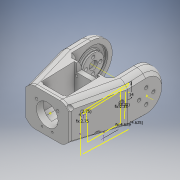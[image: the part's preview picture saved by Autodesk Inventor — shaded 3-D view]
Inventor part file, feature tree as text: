
AUTODESK INVENTOR PART (.ipt)
format: ipt  version: 2018 (Build 220112000, 112)  size: 1,037,312 bytes
history: native  units: mm
features: projected_geometry x48, sketch x44, extrude x36, hole x13, other x10, chamfer x9, fillet x7, reference x3, mirror x1, plane x1
ambient origin geometry x8: Origin, YZ Plane, XZ Plane, XY Plane, X Axis, Y Axis, Z Axis, Center Point
bodies: Solid1 (feature_tree)
feature tree (172):
  extrude  "Extrusion1"  Depth=45.0mm
  extrude  "Extrusion2"  Depth=2.25mm
  hole  "Hole1"  [1 undecoded]
  hole  "Hole2"  [1 undecoded]
  fillet  "Fillet1"  Radius=14.0mm
  extrude  "Extrusion3"  Depth=18.5mm
  extrude  "Extrusion4"  Depth=10.0mm
  extrude  "Extrusion5"  Depth=2.0mm
  extrude  "Extrusion6"  Depth=2.0mm
  hole  "Hole3"  [1 undecoded]
  extrude  "Extrusion7"  Depth=2.0mm
  extrude  "Extrusion8"  Depth=1.0mm TaperAngle=0.0deg
  extrude  "Extrusion9"  Depth=24.5mm
  extrude  "Extrusion10"  Depth=10.0mm
  extrude  "Extrusion11"  Depth=14.5mm
  extrude  "Extrusion13"  Depth=14.5mm
  extrude  "Extrusion14"  Depth=5.0mm
  extrude  "Extrusion15"  Depth=2.25mm
  extrude  "Extrusion16"  Depth=5.0mm
  extrude  "Extrusion17"  Depth=9.0mm
  chamfer  "Chamfer1"  Distance=1.0mm
  fillet  "Fillet7"  Radius=20.7mm
  fillet  "Fillet8"  Radius=32.0mm
  mirror  "Mirror1"
  sketch  "Sketch26"  dims[d55=2.25mm d56=5.0mm]
  extrude  "Extrusion24"  Depth=1.0mm TaperAngle=0.0deg
  extrude  "Extrusion25"  Depth=8.0mm
  extrude  "Extrusion26"  Depth=0.2mm TaperAngle=0.0deg
  extrude  "Extrusion27"  Depth=5.0mm TaperAngle=0.0deg
  other  "Work Axis1"
  plane  "Work Plane2"
  extrude  "Extrusion28"  Depth=0.2mm TaperAngle=0.0deg
  extrude  "Extrusion29"  Depth=2.0mm TaperAngle=45.0deg
  chamfer  "Chamfer2"  Distance=15.0mm
  extrude  "Extrusion31"  Depth=15.0mm TaperAngle=0.0deg
  chamfer  "Chamfer3"  Distance=15.0mm
  chamfer  "Chamfer4"  Distance=100.0mm
  extrude  "Extrusion32"  Depth=2.0mm TaperAngle=0.0deg
  chamfer  "Chamfer5"  Distance=6.0mm Angle=45.0deg
  extrude  "Extrusion33"  TaperAngle=0.0deg  [1 undecoded]
  sketch  "Sketch41"  dims[d100=0.2mm d101=0.0mm d102=2.5mm d103=2.0mm d104=45.0deg]
  extrude  "Extrusion34"  Depth=2.0mm
  chamfer  "Chamfer6"  Distance=11.5mm
  fillet  "Fillet9"  Radius=11.5mm
  extrude  "Extrusion35"  Depth=2.0mm TaperAngle=0.0deg
  extrude  "Extrusion36"  Depth=2.0mm TaperAngle=45.0deg
  chamfer  "Chamfer7"  Distance=2.0mm Angle=45.0deg
  fillet  "Fillet10"  Radius=7.0mm
  extrude  "Extrusion37"  Depth=2.0mm TaperAngle=0.0deg
  extrude  "Extrusion38"  Depth=2.0mm TaperAngle=45.0deg
  extrude  "Extrusion39"  Depth=2.0mm TaperAngle=0.0deg
  extrude  "Extrusion40"  Depth=2.0mm TaperAngle=0.0deg
  chamfer  "Chamfer8"  Distance=2.0mm Angle=45.0deg
  chamfer  "Chamfer9"  Distance=8.0mm
  hole  "Hole6"  [1 undecoded]
  fillet  "Fillet11"  Radius=10.970628mm
  fillet  "Fillet12"  Radius=15.470628mm
  extrude  "Extrusion41"  Depth=2.0mm TaperAngle=0.0deg
  extrude  "Extrusion42"  Depth=2.0mm TaperAngle=0.0deg
  hole  "Hole7"  [1 undecoded]
  extrude  "Extrusion43"  Depth=2.0mm
  extrude  "Extrusion44"  TaperAngle=15.0deg  [1 undecoded]
  sketch  "Sketch58"  dims[d162=5.0mm d165=100.0mm d166=0.0mm d167=100.0mm d168=0.0mm d169=6.0mm d170=2.0mm d171=45.0deg d172=0.0mm d173=11.5mm d175=11.5mm d176=11.5mm d179=100.0mm d180=0.0mm d181=5.0mm d182=2.0mm d183=45.0deg d184=5.0mm d185=2.0mm d186=45.0deg d187=7.0mm d188=100.0mm d189=0.0mm d190=5.0mm d191=2.0mm d192=45.0deg d193=100.0mm d194=0.0mm d195=100.0mm d196=0.0mm d197=5.0mm d198=2.0mm d199=45.0deg d200=8.0mm d202=15.0deg d204=10.970628mm d205=15.470628mm d206=2.5mm d207=0.0mm d208=2.5mm d209=0.0mm d210=3.0mm d211=2.0mm d212=45.0deg d213=2.0mm d215=15.0deg d216=4.0mm d217=4.0mm d218=5.0mm d219=0.0mm d222=32.0mm d223=4.0mm d224=0.0mm d225=2.5mm d226=0.0mm d227=6.5mm d228=0.0mm d229=3.0mm d230=2.0mm d231=45.0deg d232=3.0mm d233=2.0mm d234=45.0deg d235=1.567mm d236=15.0mm d237=4.0mm d238=2.0mm d239=90.0deg d240=15.0mm d241=20.594885mm d242=2.0mm d243=0.75mm d244=20.5mm d245=3.05mm d246=0.0mm d247=14.0mm d248=3.2mm d249=6.0mm d250=4.0mm d251=2.0mm d252=90.0deg d253=8.8mm d254=20.594885mm d255=20.5mm d256=1.55mm d257=0.0mm d258=8.0mm d259=2.5mm d260=0.0mm d261=8.0mm d262=2.5mm d263=0.0mm d266=4.624622mm d267=4.624622mm d268=2.75mm d269=2.75mm d270=2.35mm d271=2.35mm d272=14.0mm d273=4.0mm d274=5.6mm d275=3.708mm d276=3.023mm d277=2.0mm d278=14.3117mm d279=17.0mm d280=0.0mm d281=4.0mm d282=3.708mm d283=3.023mm d284=2.0mm d285=14.3117mm d286=19.0mm d287=0.0mm d288=4.0mm d289=3.708mm d290=3.023mm d291=2.0mm d292=14.3117mm d293=13.0mm d294=0.0mm d295=2.3mm d296=4.0mm d297=4.4mm d298=2.0mm d299=90.0deg d300=32.25mm d301=0.0mm d302=3.3mm d303=4.0mm d304=6.3mm d305=2.0mm d306=90.0deg d307=32.25mm d308=0.0mm d309=1.567mm d310=4.0mm d311=6.3mm d312=2.0mm d313=90.0deg d314=45.0mm d315=20.594885mm d316=1.567mm d317=4.0mm d318=6.3mm d319=2.0mm d320=90.0deg d321=55.0mm d322=20.594885mm d323=2.459mm d324=6.0mm d325=6.3mm d326=2.0mm d327=90.0deg d328=50.0mm d329=20.594885mm]
  hole  "Hole8"  [1 undecoded]
  hole  "Hole9"  [1 undecoded]
  hole  "Hole10"  [1 undecoded]
  hole  "Hole11"  [1 undecoded]
  hole  "Hole12"  [1 undecoded]
  hole  "Hole13"  [1 undecoded]
  hole  "Hole14"  [1 undecoded]
  hole  "Hole15"  [1 undecoded]
  sketch  "Sketch1"  dims[d0=24.5mm d1=45.0mm]
  sketch  "Sketch2"  dims[d2=1.95mm d3=0.0mm d4=2.25mm]
  projected_geometry  "Projected Loop1"
  sketch  "Sketch3"  dims[d5=20.0mm d6=2.25mm]
  projected_geometry  "Projected Loop2"
  sketch  "Sketch4"  dims[d7=5.25mm d8=5.25mm d9=14.0mm]
  projected_geometry  "Projected Loop3"
  sketch  "Sketch5"  dims[d10=5.25mm d11=18.5mm]
  projected_geometry  "Projected Loop4"
  sketch  "Sketch6"  dims[d12=10.0mm d13=0.0mm d14=20.5mm]
  projected_geometry  "Projected Loop5"
  sketch  "Sketch7"  dims[d15=2.0mm d16=2.195mm]
  projected_geometry  "Projected Loop6"
  sketch  "Sketch8"  dims[d17=2.0mm]
  projected_geometry  "Projected Loop7"
  sketch  "Sketch9"  dims[d18=2.4mm d19=6.0mm d20=4.4mm d21=2.0mm d22=90.0deg d23=8.0mm d24=20.594885mm d25=20.5mm]
  projected_geometry  "Projected Loop8"
  projected_geometry  "Projected Loop9"
  sketch  "Sketch10"  dims[d26=26.65mm d27=2.0mm]
  projected_geometry  "Projected Loop10"
  projected_geometry  "Projected Loop11"
  sketch  "Sketch11"  dims[d28=2.0mm]
  projected_geometry  "Projected Loop12"
  sketch  "Sketch12"  dims[d29=2.4mm d30=6.0mm d31=4.4mm d32=2.0mm d33=90.0deg d34=8.0mm d35=20.594885mm d36=0.5mm]
  sketch  "Sketch13"  dims[d37=18.0mm d38=1.0mm d39=0.0mm]
  sketch  "Sketch14"  dims[d41=5.0mm d42=0.0mm d43=24.5mm]
  projected_geometry  "Projected Loop13"
  sketch  "Sketch16"  dims[d44=1.15mm d45=0.0mm d46=10.0mm]
  projected_geometry  "Projected Loop14"
  sketch  "Sketch17"  dims[d47=21.0mm d48=14.5mm]
  projected_geometry  "Projected Loop15"
  sketch  "Sketch18"  dims[d49=20.0mm d50=14.5mm]
  projected_geometry  "Projected Loop16"
  sketch  "Sketch19"  dims[d51=24.5mm d52=5.0mm]
  projected_geometry  "Projected Loop17"
  sketch  "Sketch20"  dims[d53=5.0mm d54=2.25mm]
  projected_geometry  "Projected Loop18"
  projected_geometry  "Projected Loop25"
  sketch  "Sketch31"  dims[d57=5.0mm d58=9.0mm]
  projected_geometry  "Projected Loop30"
  reference  "Reference1"
  sketch  "Sketch32"  dims[d59=14.75mm]
  projected_geometry  "Projected Loop31"
  sketch  "Sketch33"  dims[d60=4.0mm d61=1.0mm d62=0.0mm d63=20.7mm]
  projected_geometry  "Projected Loop32"
  sketch  "Sketch34"  dims[d64=2.4mm d65=6.0mm d66=4.4mm d67=2.0mm d68=90.0deg d69=8.0mm d70=20.594885mm d72=32.0mm]
  projected_geometry  "Projected Loop33"
  other  "Work Point1"
  other  "Work Point2"
  other  "Work Point3"
  sketch  "Sketch35"  dims[d73=3.0mm d74=0.0mm d75=1.0mm d76=0.0mm]
  sketch  "Sketch37"  dims[d77=12.25mm d78=0.0mm d80=8.0mm]
  projected_geometry  "Projected Loop34"
  sketch  "Sketch38"  dims[d81=4.5mm d82=0.0mm d84=0.2mm d85=0.0mm]
  sketch  "Sketch39"  dims[d91=8.0mm d92=0.0mm d93=5.0mm d94=0.0mm]
  sketch  "Sketch40"  dims[d95=5.0mm d96=0.0mm d98=0.2mm d99=0.0mm]
  projected_geometry  "Projected Loop35"
  projected_geometry  "Projected Loop36"
  projected_geometry  "Projected Loop37"
  projected_geometry  "Projected Loop38"
  sketch  "Sketch42"  dims[d105=1.5mm]
  projected_geometry  "Projected Loop39"
  sketch  "Sketch43"  dims[d114=0.5mm]
  reference  "Reference2"
  reference  "Reference3"
  sketch  "Sketch45"  dims[d130=60.0mm]
  projected_geometry  "Projected Loop40"
  sketch  "Sketch46"  dims[d131=36.0mm]
  projected_geometry  "Projected Loop41"
  sketch  "Sketch48"  dims[d146=40.0mm]
  projected_geometry  "Projected Loop43"
  sketch  "Sketch49"  dims[d147=60.0mm]
  projected_geometry  "Projected Loop44"
  projected_geometry  "Projected Loop45"
  sketch  "Sketch50"  dims[d148=0.0mm]
  projected_geometry  "Projected Loop46"
  sketch  "Sketch52"  dims[d149=2.3mm d150=15.0mm d151=0.0mm]
  sketch  "Sketch53"  dims[d152=15.0mm d153=0.0mm d154=15.0mm d155=0.0mm d156=15.0mm d157=0.0mm]
  projected_geometry  "Projected Loop47"
  sketch  "Sketch54"  dims[d158=20.5mm]
  projected_geometry  "Projected Loop48"
  sketch  "Sketch55"  dims[d159=41.5mm]
  sketch  "Sketch56"  dims[d160=15.5mm]
  projected_geometry  "Projected Loop49"
  sketch  "Sketch57"  dims[d161=15.5mm]
  projected_geometry  "Projected Loop50"
  projected_geometry  "Projected Loop51"
  projected_geometry  "Projected Loop52"
  projected_geometry  "Projected Loop53"
  projected_geometry  "Projected Loop54"
  projected_geometry  "Projected Loop55"
  projected_geometry  "Projected Loop56"
  projected_geometry  "Projected Loop57"
  parser-record x1  (decoder bookkeeping rows leaked as tree rows — omitted from the tree; the rows remain in map.json)
  other  "servocheck.iam"
  other  "LX-16A:3"
  other  "DUOPAN-SG-SJ_10"
  projected_geometry  "Project Cut Edges1"
  projected_geometry  "Project Cut Edges3"
  other  "bottomarm:1"
  other  "arm1:1"
note: 15 required parameter values undecoded (feature->parameter linkage not recoverable at this tier; creation-order binding heuristic only, values carry confidence <= 0.55)
note: 1 file-system path scrubbed to <path> (originals preserved in map.json)
